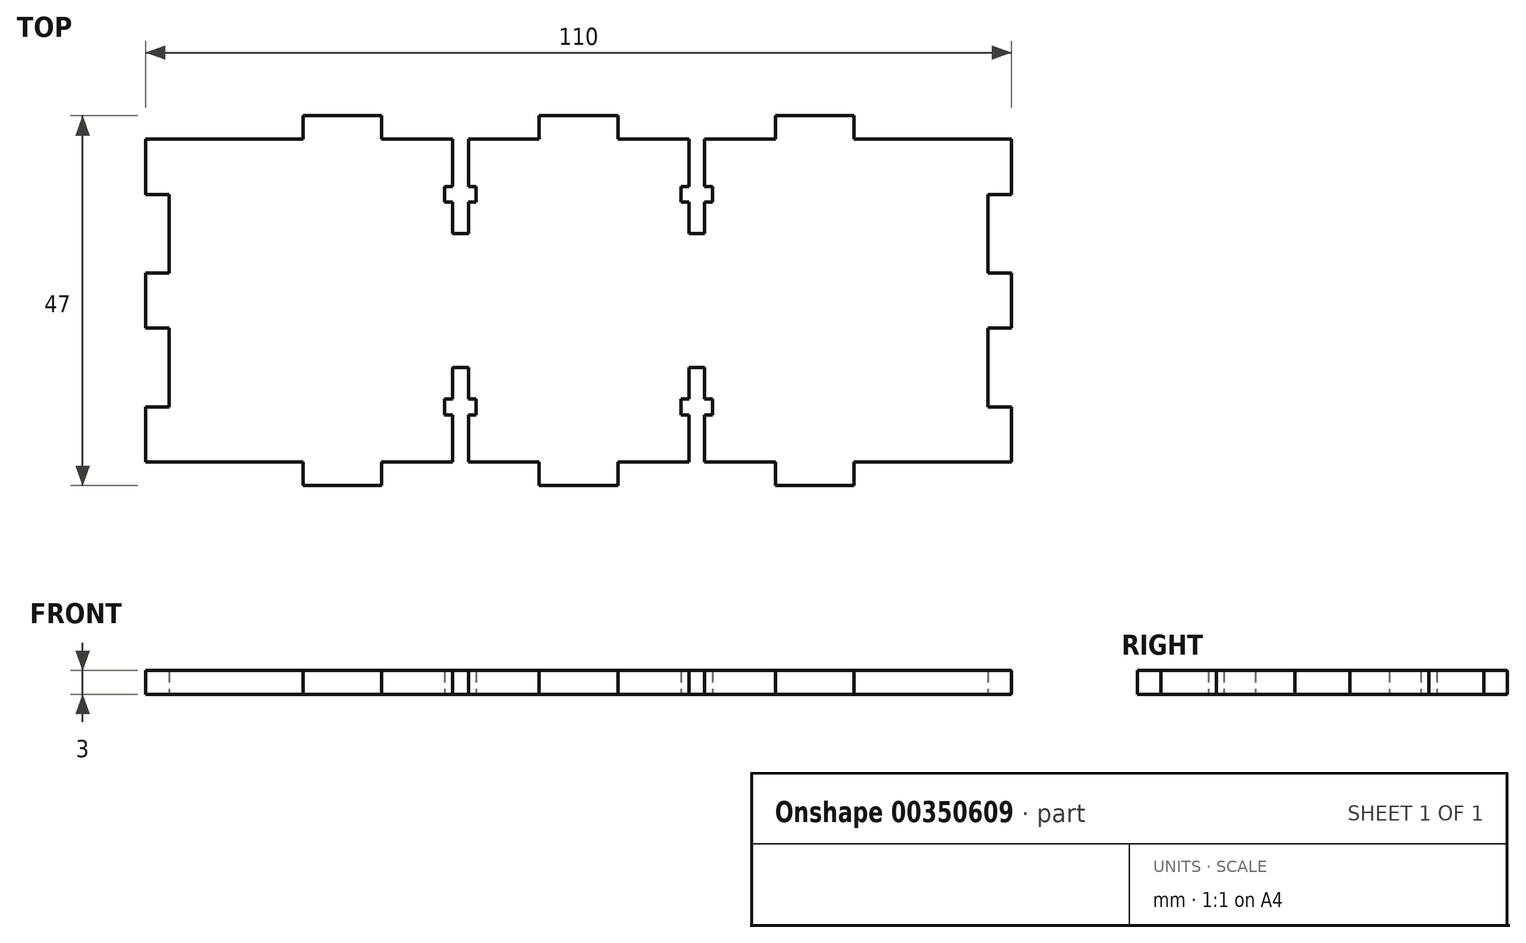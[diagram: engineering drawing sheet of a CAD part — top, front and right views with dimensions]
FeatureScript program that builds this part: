
annotation { "Feature Type Name" : "Feature", "Feature Type Description" : "" }
export const myFeature = defineFeature(function(context is Context, id is Id, definition is map)
    precondition{}
    {
        {
            var Q0;
            Q0=qCreatedBy(makeId("Top.planeOp"),FACE);
            var sketch = newSketch(context, id + "F0", { "sketchPlane" : qUnion([Q0])});
            skLineSegment(sketch, "E0", {"start": v(2.36, -15.34) * mm, "end": v(-7.64, -15.34) * mm});
            skLineSegment(sketch, "E1", {"start": v(-7.64, -15.34) * mm, "end": v(-7.64, -12.34) * mm});
            skLineSegment(sketch, "E2", {"start": v(-27.64, -12.34) * mm, "end": v(-27.64, -15.34) * mm});
            skLineSegment(sketch, "E3", {"start": v(-27.64, -15.34) * mm, "end": v(-37.64, -15.34) * mm});
            skLineSegment(sketch, "E4", {"start": v(-37.64, -15.34) * mm, "end": v(-37.64, -12.34) * mm});
            skLineSegment(sketch, "E5", {"start": v(-37.64, -12.34) * mm, "end": v(-57.64, -12.34) * mm});
            skLineSegment(sketch, "E6", {"start": v(-57.64, -12.34) * mm, "end": v(-57.64, -5.34) * mm});
            skLineSegment(sketch, "E7", {"start": v(-57.64, -5.34) * mm, "end": v(-54.64, -5.34) * mm});
            skLineSegment(sketch, "E8", {"start": v(-54.64, -5.34) * mm, "end": v(-54.64, 4.66) * mm});
            skLineSegment(sketch, "E9", {"start": v(-54.64, 4.66) * mm, "end": v(-57.64, 4.66) * mm});
            skLineSegment(sketch, "E10", {"start": v(-57.64, 4.66) * mm, "end": v(-57.64, 11.66) * mm});
            skLineSegment(sketch, "E11", {"start": v(-57.64, 11.66) * mm, "end": v(-54.64, 11.66) * mm});
            skLineSegment(sketch, "E12", {"start": v(-54.64, 11.66) * mm, "end": v(-54.64, 21.66) * mm});
            skLineSegment(sketch, "E13", {"start": v(-54.64, 21.66) * mm, "end": v(-57.64, 21.66) * mm});
            skLineSegment(sketch, "E14", {"start": v(-57.64, 21.66) * mm, "end": v(-57.64, 28.66) * mm});
            skLineSegment(sketch, "E15", {"start": v(-57.64, 28.66) * mm, "end": v(-37.64, 28.66) * mm});
            skLineSegment(sketch, "E16", {"start": v(-37.64, 28.66) * mm, "end": v(-37.64, 31.66) * mm});
            skLineSegment(sketch, "E17", {"start": v(-37.64, 31.66) * mm, "end": v(-27.64, 31.66) * mm});
            skLineSegment(sketch, "E18", {"start": v(-27.64, 31.66) * mm, "end": v(-27.64, 28.66) * mm});
            skLineSegment(sketch, "E19", {"start": v(-7.64, 28.66) * mm, "end": v(-7.64, 31.66) * mm});
            skLineSegment(sketch, "E20", {"start": v(-7.64, 31.66) * mm, "end": v(2.36, 31.66) * mm});
            skLineSegment(sketch, "E21", {"start": v(-18.64, -12.34) * mm, "end": v(-18.64, -6.34) * mm});
            skLineSegment(sketch, "E22", {"start": v(-18.64, -6.34) * mm, "end": v(-19.64, -6.34) * mm});
            skLineSegment(sketch, "E23", {"start": v(-19.64, -6.34) * mm, "end": v(-19.64, -4.34) * mm});
            skLineSegment(sketch, "E24", {"start": v(-19.64, -4.34) * mm, "end": v(-18.64, -4.34) * mm});
            skLineSegment(sketch, "E25", {"start": v(-18.64, -4.34) * mm, "end": v(-18.64, -0.34) * mm});
            skLineSegment(sketch, "E26", {"start": v(-18.64, -0.34) * mm, "end": v(-16.64, -0.34) * mm});
            skLineSegment(sketch, "E27", {"start": v(-16.64, -0.34) * mm, "end": v(-16.64, -4.34) * mm});
            skLineSegment(sketch, "E28", {"start": v(-16.64, -4.34) * mm, "end": v(-15.64, -4.34) * mm});
            skLineSegment(sketch, "E29", {"start": v(-15.64, -4.34) * mm, "end": v(-15.64, -6.34) * mm});
            skLineSegment(sketch, "E30", {"start": v(-15.64, -6.34) * mm, "end": v(-16.64, -6.34) * mm});
            skLineSegment(sketch, "E31", {"start": v(-16.64, -6.34) * mm, "end": v(-16.64, -12.34) * mm});
            skLineSegment(sketch, "E32.MirrorCS", {"start": v(-15.64, 22.66) * mm, "end": v(-16.64, 22.66) * mm});
            skLineSegment(sketch, "E33.MirrorCS", {"start": v(-16.64, 20.66) * mm, "end": v(-15.64, 20.66) * mm});
            skLineSegment(sketch, "E34.MirrorCS", {"start": v(-19.64, 20.66) * mm, "end": v(-18.64, 20.66) * mm});
            skLineSegment(sketch, "E35.MirrorCS", {"start": v(-18.64, 22.66) * mm, "end": v(-19.64, 22.66) * mm});
            skLineSegment(sketch, "E36.MirrorCS", {"start": v(-16.64, 16.66) * mm, "end": v(-16.64, 20.66) * mm});
            skLineSegment(sketch, "E37.MirrorCS", {"start": v(-18.64, 16.66) * mm, "end": v(-16.64, 16.66) * mm});
            skLineSegment(sketch, "E38.MirrorCS", {"start": v(-19.64, 22.66) * mm, "end": v(-19.64, 20.66) * mm});
            skLineSegment(sketch, "E39.MirrorCS", {"start": v(-18.64, 20.66) * mm, "end": v(-18.64, 16.66) * mm});
            skLineSegment(sketch, "E40.MirrorCS", {"start": v(-18.64, 28.66) * mm, "end": v(-18.64, 22.66) * mm});
            skLineSegment(sketch, "E41.MirrorCS", {"start": v(-16.64, 22.66) * mm, "end": v(-16.64, 28.66) * mm});
            skLineSegment(sketch, "E42.MirrorCS", {"start": v(-15.64, 20.66) * mm, "end": v(-15.64, 22.66) * mm});
            skLineSegment(sketch, "E43", {"start": v(-27.64, 28.66) * mm, "end": v(-18.64, 28.66) * mm});
            skLineSegment(sketch, "E44", {"start": v(-16.64, 28.66) * mm, "end": v(-7.64, 28.66) * mm});
            skLineSegment(sketch, "E45", {"start": v(-27.64, -12.34) * mm, "end": v(-18.64, -12.34) * mm});
            skLineSegment(sketch, "E46", {"start": v(-2.64, -15.34) * mm, "end": v(-2.64, 31.66) * mm, "construction": true});
            skLineSegment(sketch, "E47", {"start": v(-16.64, -12.34) * mm, "end": v(-7.64, -12.34) * mm});
            skLineSegment(sketch, "E48", {"start": v(0, -21.06) * mm, "end": v(4.66, -21.06) * mm});
            skLineSegment(sketch, "E49.MirrorCS", {"start": v(14.36, 20.66) * mm, "end": v(13.36, 20.66) * mm});
            skLineSegment(sketch, "E50.MirrorCS", {"start": v(14.36, -4.34) * mm, "end": v(13.36, -4.34) * mm});
            skLineSegment(sketch, "E51.MirrorCS", {"start": v(14.36, -6.34) * mm, "end": v(14.36, -4.34) * mm});
            skLineSegment(sketch, "E52.MirrorCS", {"start": v(10.36, 22.66) * mm, "end": v(11.36, 22.66) * mm});
            skLineSegment(sketch, "E53.MirrorCS", {"start": v(13.36, -0.34) * mm, "end": v(11.36, -0.34) * mm});
            skLineSegment(sketch, "E54.MirrorCS", {"start": v(11.36, -4.34) * mm, "end": v(10.36, -4.34) * mm});
            skLineSegment(sketch, "E55.MirrorCS", {"start": v(10.36, 20.66) * mm, "end": v(10.36, 22.66) * mm});
            skLineSegment(sketch, "E56.MirrorCS", {"start": v(13.36, -6.34) * mm, "end": v(14.36, -6.34) * mm});
            skLineSegment(sketch, "E57.MirrorCS", {"start": v(10.36, -4.34) * mm, "end": v(10.36, -6.34) * mm});
            skLineSegment(sketch, "E58.MirrorCS", {"start": v(14.36, 22.66) * mm, "end": v(14.36, 20.66) * mm});
            skLineSegment(sketch, "E59.MirrorCS", {"start": v(13.36, 16.66) * mm, "end": v(11.36, 16.66) * mm});
            skLineSegment(sketch, "E60.MirrorCS", {"start": v(13.36, 22.66) * mm, "end": v(14.36, 22.66) * mm});
            skLineSegment(sketch, "E61.MirrorCS", {"start": v(11.36, 20.66) * mm, "end": v(10.36, 20.66) * mm});
            skLineSegment(sketch, "E62.MirrorCS", {"start": v(10.36, -6.34) * mm, "end": v(11.36, -6.34) * mm});
            skLineSegment(sketch, "E63.MirrorCS", {"start": v(11.36, -0.34) * mm, "end": v(11.36, -4.34) * mm});
            skLineSegment(sketch, "E64.MirrorCS", {"start": v(32.36, 31.66) * mm, "end": v(22.36, 31.66) * mm});
            skLineSegment(sketch, "E65.MirrorCS", {"start": v(11.36, 22.66) * mm, "end": v(11.36, 28.66) * mm});
            skLineSegment(sketch, "E66.MirrorCS", {"start": v(13.36, -4.34) * mm, "end": v(13.36, -0.34) * mm});
            skLineSegment(sketch, "E67.MirrorCS", {"start": v(52.36, -5.34) * mm, "end": v(49.36, -5.34) * mm});
            skLineSegment(sketch, "E68.MirrorCS", {"start": v(49.36, 4.66) * mm, "end": v(52.36, 4.66) * mm});
            skLineSegment(sketch, "E69.MirrorCS", {"start": v(13.36, 20.66) * mm, "end": v(13.36, 16.66) * mm});
            skLineSegment(sketch, "E70.MirrorCS", {"start": v(32.36, 28.66) * mm, "end": v(32.36, 31.66) * mm});
            skLineSegment(sketch, "E71.MirrorCS", {"start": v(22.36, 31.66) * mm, "end": v(22.36, 28.66) * mm});
            skLineSegment(sketch, "E72.MirrorCS", {"start": v(52.36, 4.66) * mm, "end": v(52.36, 11.66) * mm});
            skLineSegment(sketch, "E73.MirrorCS", {"start": v(49.36, 11.66) * mm, "end": v(49.36, 21.66) * mm});
            skLineSegment(sketch, "E74.MirrorCS", {"start": v(49.36, -5.34) * mm, "end": v(49.36, 4.66) * mm});
            skLineSegment(sketch, "E75.MirrorCS", {"start": v(11.36, 28.66) * mm, "end": v(2.36, 28.66) * mm});
            skLineSegment(sketch, "E76.MirrorCS", {"start": v(11.36, 16.66) * mm, "end": v(11.36, 20.66) * mm});
            skLineSegment(sketch, "E77.MirrorCS", {"start": v(11.36, -6.34) * mm, "end": v(11.36, -12.34) * mm});
            skLineSegment(sketch, "E78.MirrorCS", {"start": v(49.36, 21.66) * mm, "end": v(52.36, 21.66) * mm});
            skLineSegment(sketch, "E79.MirrorCS", {"start": v(22.36, -12.34) * mm, "end": v(13.36, -12.34) * mm});
            skLineSegment(sketch, "E80.MirrorCS", {"start": v(2.36, 28.66) * mm, "end": v(2.36, 31.66) * mm});
            skLineSegment(sketch, "E81.MirrorCS", {"start": v(52.36, 11.66) * mm, "end": v(49.36, 11.66) * mm});
            skLineSegment(sketch, "E82.MirrorCS", {"start": v(13.36, 28.66) * mm, "end": v(13.36, 22.66) * mm});
            skLineSegment(sketch, "E83.MirrorCS", {"start": v(52.36, -12.34) * mm, "end": v(52.36, -5.34) * mm});
            skLineSegment(sketch, "E84.MirrorCS", {"start": v(22.36, -15.34) * mm, "end": v(32.36, -15.34) * mm});
            skLineSegment(sketch, "E85.MirrorCS", {"start": v(32.36, -12.34) * mm, "end": v(52.36, -12.34) * mm});
            skLineSegment(sketch, "E86.MirrorCS", {"start": v(52.36, 28.66) * mm, "end": v(32.36, 28.66) * mm});
            skLineSegment(sketch, "E87.MirrorCS", {"start": v(22.36, 28.66) * mm, "end": v(13.36, 28.66) * mm});
            skLineSegment(sketch, "E88.MirrorCS", {"start": v(22.36, -12.34) * mm, "end": v(22.36, -15.34) * mm});
            skLineSegment(sketch, "E89.MirrorCS", {"start": v(52.36, 21.66) * mm, "end": v(52.36, 28.66) * mm});
            skLineSegment(sketch, "E90.MirrorCS", {"start": v(32.36, -15.34) * mm, "end": v(32.36, -12.34) * mm});
            skLineSegment(sketch, "E91.MirrorCS", {"start": v(2.36, -15.34) * mm, "end": v(2.36, -12.34) * mm});
            skLineSegment(sketch, "E92.MirrorCS", {"start": v(11.36, -12.34) * mm, "end": v(2.36, -12.34) * mm});
            skLineSegment(sketch, "E93.MirrorCS", {"start": v(13.36, -12.34) * mm, "end": v(13.36, -6.34) * mm});
            skSolve(sketch);
        }
        {
            var Q0;
            Q0=makeQuery(id+"F0.imprint","IMPRINT",FACE,{"disambiguationData":[TD([[makeQuery(id+"F0.imprint","IMPRINT",EDGE,{"derivedFrom":sQuery(id+"F0.wireOp",EDGE,"yufxOizK-kAsC-njTP-H5ou-Tlvl3dEBZiF1")}),1.0]])]});
            var Q1;
            Q1=makeQuery(id+"F0.imprint","IMPRINT",FACE,{"disambiguationData":[TD([[makeQuery(id+"F0.imprint","IMPRINT",EDGE,{"derivedFrom":sQuery(id+"F0.wireOp",EDGE,"E0")}),-1.0]])]});
            extrude(context, id + "F1", {"entities" : qUnion([Q0, Q1]), "depth" : 3 * mm});
        }
    });
